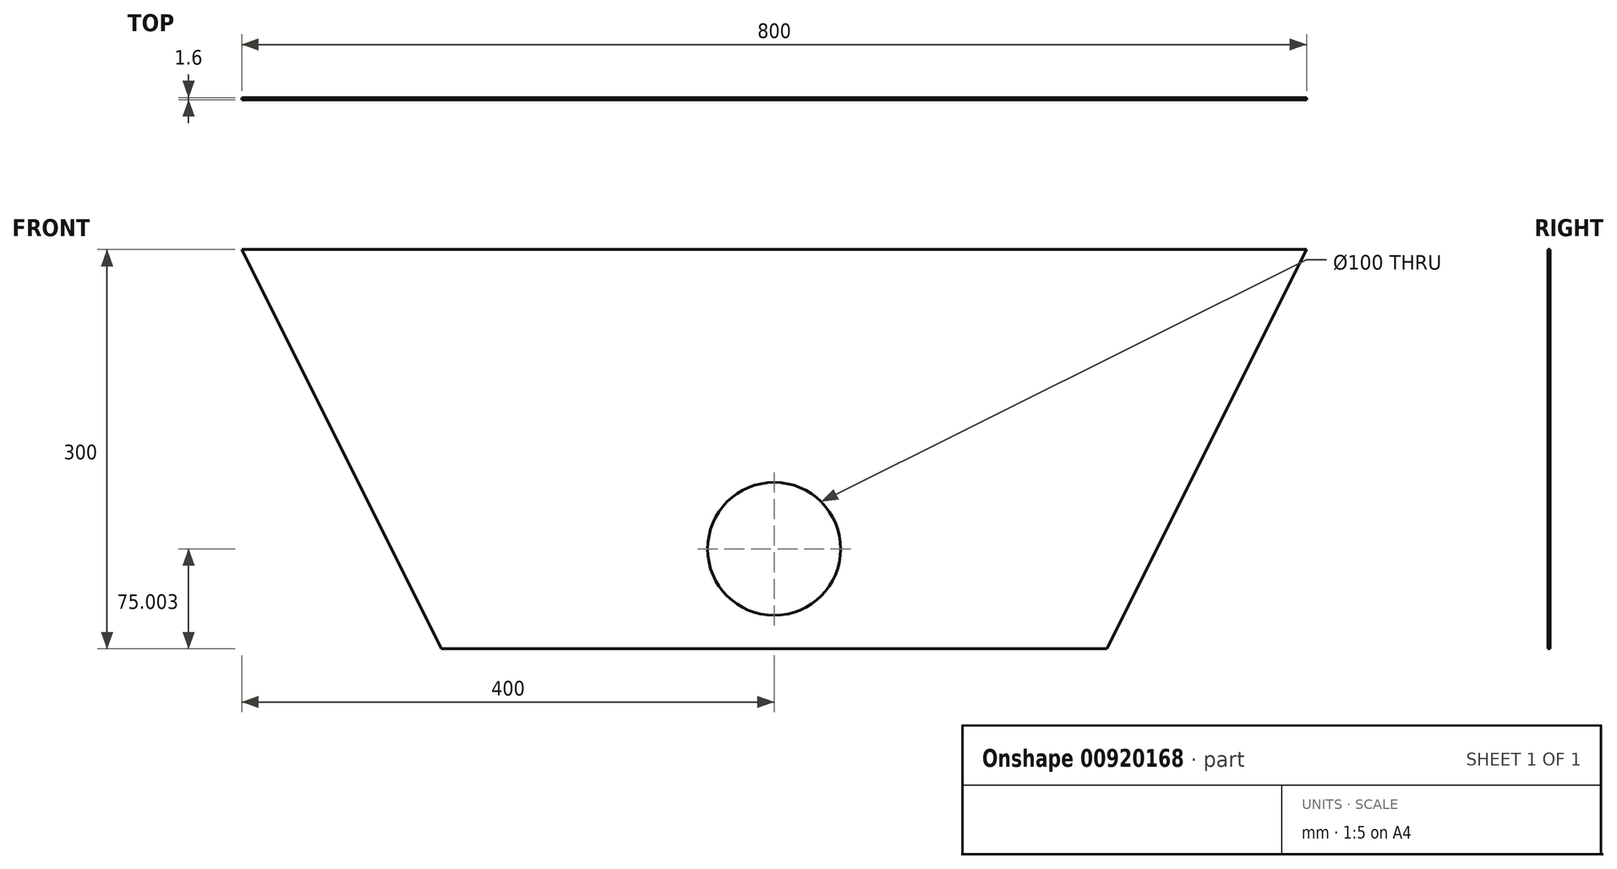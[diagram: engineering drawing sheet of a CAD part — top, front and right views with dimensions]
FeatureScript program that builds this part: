
annotation { "Feature Type Name" : "Feature", "Feature Type Description" : "" }
export const myFeature = defineFeature(function(context is Context, id is Id, definition is map)
    precondition{}
    {
        {
            var Q0;
            Q0=qCreatedBy(makeId("Front.planeOp"),FACE);
            var sketch = newSketch(context, id + "F0", { "sketchPlane" : qUnion([Q0])});
            skLineSegment(sketch, "E0", {"start": v(-250, -214.06) * mm, "end": v(250, -214.06) * mm});
            skLineSegment(sketch, "E1", {"start": v(399.2, 84.34) * mm, "end": v(250, -214.06) * mm});
            skLineSegment(sketch, "E2", {"start": v(-399.2, 84.34) * mm, "end": v(-250, -214.06) * mm});
            skLineSegment(sketch, "E3", {"start": v(-400, 85.94) * mm, "end": v(-399.2, 84.34) * mm});
            skLineSegment(sketch, "E4", {"start": v(399.2, 84.34) * mm, "end": v(400, 85.94) * mm});
            skLineSegment(sketch, "E5", {"start": v(400, 85.94) * mm, "end": v(-400, 85.94) * mm});
            skCircle(sketch, "E6", {"center": v(0, -139.06) * mm, "radius": 50 * mm});
            skPoint(sketch, "E7.start.orphan", {"position": v(0, -214.06) * mm});
            skSolve(sketch);
        }
        {
            var Q0;
            Q0=qSketchRegion(id+"F0",true);
            extrude(context, id + "F1", {"entities" : qUnion([Q0]), "depth" : 1.6 * mm, "offsetDistance" : 25 * mm});
        }
    });
